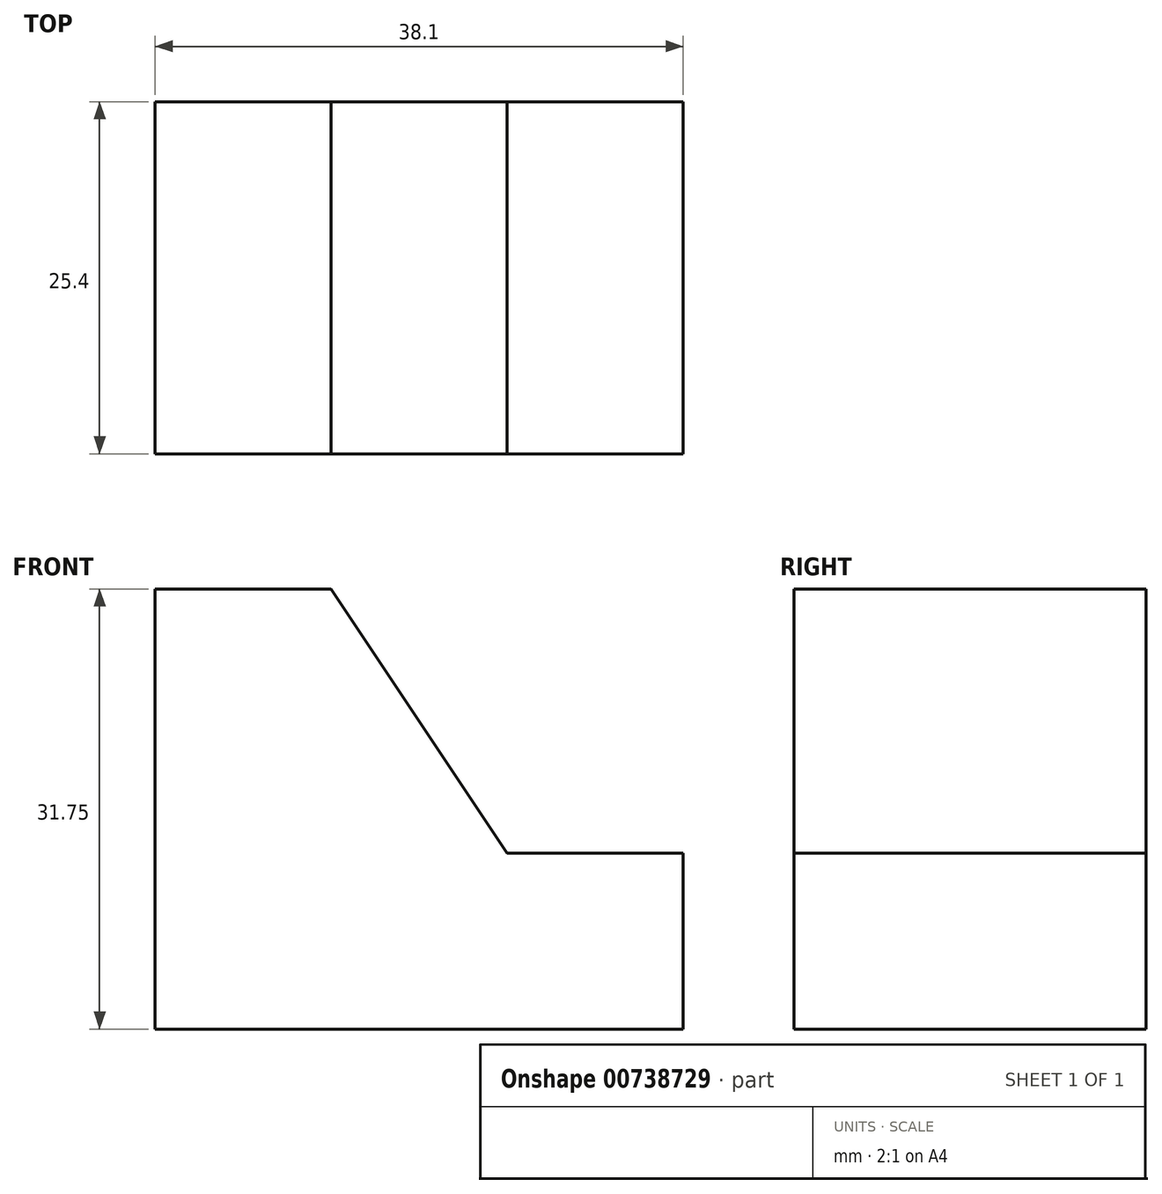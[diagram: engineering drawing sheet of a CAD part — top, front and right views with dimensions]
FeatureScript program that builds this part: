
annotation { "Feature Type Name" : "Feature", "Feature Type Description" : "" }
export const myFeature = defineFeature(function(context is Context, id is Id, definition is map)
    precondition{}
    {
        {
            var Q0;
            Q0=qCreatedBy(makeId("Front.planeOp"),FACE);
            var sketch = newSketch(context, id + "F0", { "sketchPlane" : qUnion([Q0])});
            skLineSegment(sketch, "E0", {"start": v(0, 0) * mm, "end": v(38.1, 0) * mm});
            skLineSegment(sketch, "E1", {"start": v(38.1, 0) * mm, "end": v(38.1, 12.7) * mm});
            skLineSegment(sketch, "E2", {"start": v(38.1, 12.7) * mm, "end": v(25.4, 12.7) * mm});
            skLineSegment(sketch, "E3", {"start": v(25.4, 12.7) * mm, "end": v(12.7, 31.75) * mm});
            skLineSegment(sketch, "E4", {"start": v(12.7, 31.75) * mm, "end": v(0, 31.75) * mm});
            skLineSegment(sketch, "E5", {"start": v(0, 31.75) * mm, "end": v(0, 0) * mm});
            skSolve(sketch);
        }
        {
            var Q0;
            Q0 = qSketchRegion(id + "F0", true);
            extrude(context, id + "F1", {"entities" : qUnion([Q0]), "depth" : 25.4 * mm, "offsetDistance" : 25.4 * mm});
        }
    });
